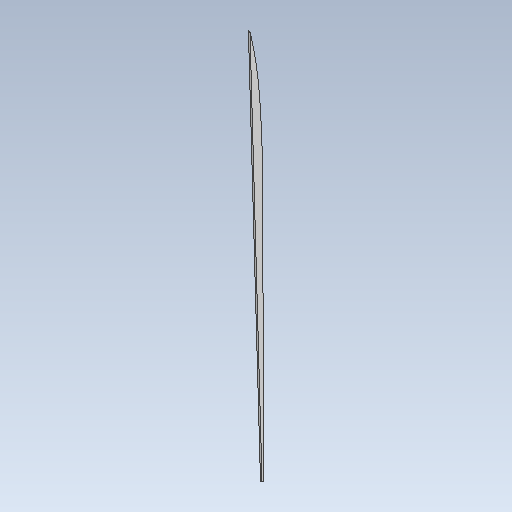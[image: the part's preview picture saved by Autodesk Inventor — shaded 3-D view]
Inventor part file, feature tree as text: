
AUTODESK INVENTOR PART (.ipt)
format: ipt  version: 2020.3 (Build 243373010, 373A)  size: 174,080 bytes
history: native  units: mm
features: other x33, extrude x1
ambient origin geometry x8: Origin, YZ Plane, XZ Plane, XY Plane, X Axis, Y Axis, Z Axis, Center Point
bodies: Solid1 (feature_tree)
feature tree (34):
  other  "base_sketch.ipt"
  extrude  "Extrusion1"  Depth=10.0mm
  other  "stringer"
  other  "stringer_inside"
  other  "bulkhead_main"
  other  "bulkhead_F1"
  other  "bulkhead_front"
  other  "bulkhead_F2"
  other  "bulkhead_B1"
  other  "bulkhead_B2"
  other  "transom"
  other  "stinger_bottom_liner"
  other  "bulkhead_front_tunnel_top"
  other  "bulkhead_front_tunnel_bottom"
  other  "bulkhead_main_top"
  other  "bulkhead_main_tunnel_bottom"
  other  "bulkhead_main_tunnel_standoff"
  other  "bulkhead_front_top"
  other  "bulkhead_front_bottom"
  other  "bulkhead_F1_tunnel_bottom"
  other  "bulkhead_F1_tunnel_top"
  other  "bulkhead_F1_top"
  other  "bulkhead_F1_tunnel_standoff"
  other  "bulkhead_F1_bottom"
  other  "bulkhead_F2_bottom"
  other  "bulkhead_F2_top"
  other  "bulkhead_B1_bottom"
  other  "bulkhead_B1_top"
  other  "bulkhead_B1_tunnel_standoff"
  other  "bulkhead_B1_tunnel_bottom"
  other  "bulkhead_B2_top"
  other  "bulkhead_B2_tunnel_bottom"
  other  "bulkhead_B2_bottom"
  other  "profile"
